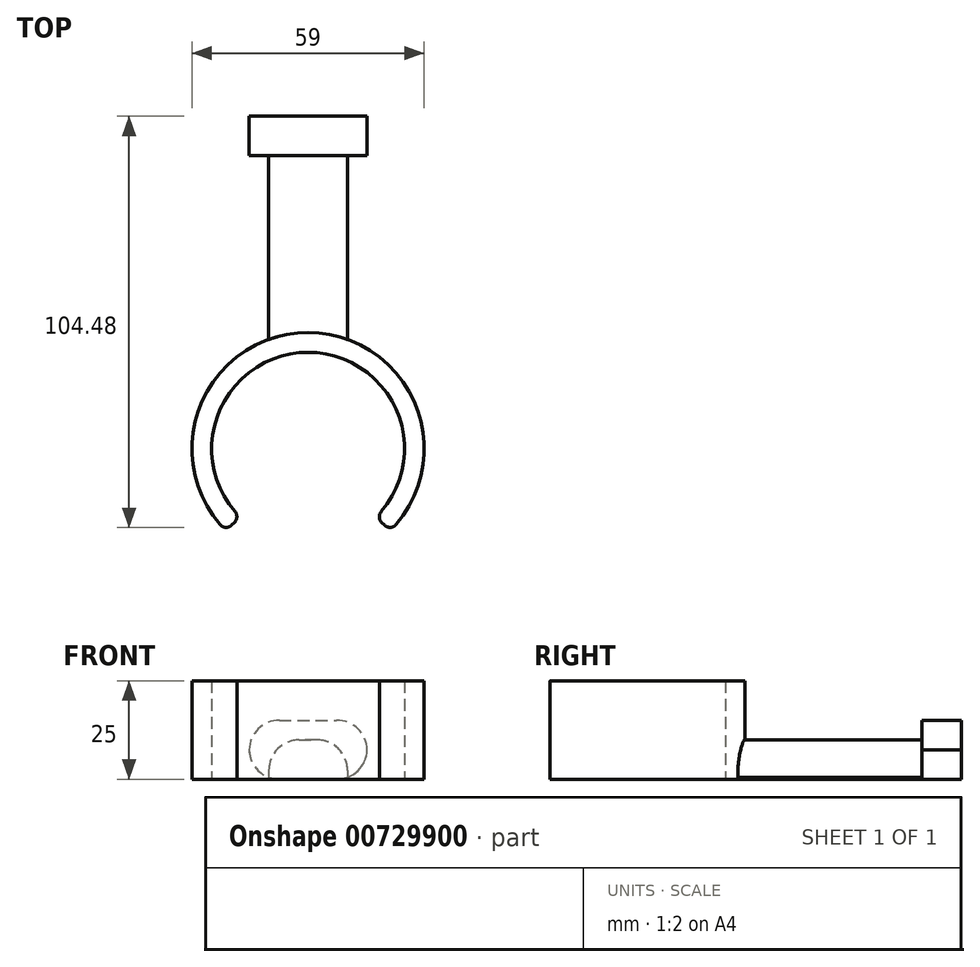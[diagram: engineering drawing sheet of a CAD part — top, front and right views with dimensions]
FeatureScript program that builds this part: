
annotation { "Feature Type Name" : "Feature", "Feature Type Description" : "" }
export const myFeature = defineFeature(function(context is Context, id is Id, definition is map)
    precondition{}
    {
        {
            var Q0;
            Q0=qCreatedBy(makeId("Top.planeOp"),FACE);
            var sketch = newSketch(context, id + "F0", { "sketchPlane" : qUnion([Q0])});
            skCircle(sketch, "E0", {"center": v(0, 0) * mm, "radius": 24.5 * mm});
            skCircle(sketch, "E1.0", {"center": v(0, 0) * mm, "radius": 29.5 * mm});
            skLineSegment(sketch, "E2.bottom", {"start": v(-10, 0) * mm, "end": v(10, 0) * mm});
            skLineSegment(sketch, "E2.top", {"start": v(-10, 74.5) * mm, "end": v(10, 74.5) * mm});
            skLineSegment(sketch, "E2.left", {"start": v(-10, 0) * mm, "end": v(-10, 74.5) * mm});
            skLineSegment(sketch, "E2.right", {"start": v(10, 0) * mm, "end": v(10, 74.5) * mm});
            skLineSegment(sketch, "E3", {"start": v(0, 0) * mm, "end": v(49.81, -49.81) * mm});
            skLineSegment(sketch, "E4", {"start": v(49.81, -49.81) * mm, "end": v(-49.81, -49.81) * mm});
            skLineSegment(sketch, "E5", {"start": v(-49.81, -49.81) * mm, "end": v(0, 0) * mm});
            skLineSegment(sketch, "E6.bottom", {"start": v(-15, 74.5) * mm, "end": v(15, 74.5) * mm});
            skLineSegment(sketch, "E6.top", {"start": v(-15, 84.5) * mm, "end": v(15, 84.5) * mm});
            skLineSegment(sketch, "E6.left", {"start": v(-15, 74.5) * mm, "end": v(-15, 84.5) * mm});
            skLineSegment(sketch, "E6.right", {"start": v(15, 74.5) * mm, "end": v(15, 84.5) * mm});
            skSolve(sketch);
        }
        {
            var Q0;
            {var subQ0=sQuery(id+"F0.wireOp",EDGE,"E2.right");var subQ1=sQuery(id+"F0.wireOp",EDGE,"E0");var subQ2=makeQuery(id+"F0.imprint","INTERSECT",VERTEX,{"derivedFrom":[subQ1,subQ0]});Q0=makeQuery(id+"F0.imprint","IMPRINT",FACE,{"disambiguationData":[TD([[makeQuery(id+"F0.imprint","IMPRINT",EDGE,{"disambiguationData":[TD([[subQ2,1.0]])],"derivedFrom":subQ1}),-1.0]])]});}
            var Q1;
            {var subQ0=sQuery(id+"F0.wireOp",EDGE,"E2.left");var subQ1=sQuery(id+"F0.wireOp",EDGE,"E0");var subQ2=makeQuery(id+"F0.imprint","INTERSECT",VERTEX,{"derivedFrom":[subQ1,subQ0]});Q1=makeQuery(id+"F0.imprint","IMPRINT",FACE,{"disambiguationData":[TD([[makeQuery(id+"F0.imprint","IMPRINT",EDGE,{"disambiguationData":[TD([[subQ2,1.0]])],"derivedFrom":subQ1}),-1.0]])]});}
            var Q2;
            {var subQ0=sQuery(id+"F0.wireOp",EDGE,"E2.left");var subQ1=sQuery(id+"F0.wireOp",EDGE,"E0");var subQ2=makeQuery(id+"F0.imprint","INTERSECT",VERTEX,{"derivedFrom":[subQ1,subQ0]});Q2=makeQuery(id+"F0.imprint","IMPRINT",FACE,{"disambiguationData":[TD([[makeQuery(id+"F0.imprint","IMPRINT",EDGE,{"disambiguationData":[TD([[subQ2,-1.0]])],"derivedFrom":subQ1}),-1.0]])]});}
            extrude(context, id + "F1", {"entities" : qUnion([Q0, Q1, Q2]), "depth" : 25 * mm, "offsetDistance" : 25 * mm});
        }
        {
            var Q0;
            Q0=makeQuery(id+"F1.opExtrude","SWEPT_EDGE",EDGE,{"disambiguationData":[OSD([sQuery(id+"F0.wireOp",EDGE,"E1.0"),sQuery(id+"F0.wireOp",EDGE,"E5")])]});
            var Q1;
            Q1=makeQuery(id+"F1.opExtrude","SWEPT_EDGE",EDGE,{"disambiguationData":[OSD([sQuery(id+"F0.wireOp",EDGE,"E0"),sQuery(id+"F0.wireOp",EDGE,"E5")])]});
            var Q2;
            Q2=makeQuery(id+"F1.opExtrude","SWEPT_EDGE",EDGE,{"disambiguationData":[OSD([sQuery(id+"F0.wireOp",EDGE,"E0"),sQuery(id+"F0.wireOp",EDGE,"E3")])]});
            var Q3;
            Q3=makeQuery(id+"F1.opExtrude","SWEPT_EDGE",EDGE,{"disambiguationData":[OSD([sQuery(id+"F0.wireOp",EDGE,"E1.0"),sQuery(id+"F0.wireOp",EDGE,"E3")])]});
            fillet(context, id + "F2", {"entities" : qUnion([Q0, Q1, Q2, Q3]), "radius" : 2 * mm, "tangentPropagation" : true, "allowEdgeOverflow" : false});
        }
        {
            var Q0;
            {var subQ0=sQuery(id+"F0.wireOp",EDGE,"E2.left");var subQ1=sQuery(id+"F0.wireOp",EDGE,"E1.0");var subQ2=makeQuery(id+"F0.imprint","INTERSECT",VERTEX,{"derivedFrom":[subQ1,subQ0]});Q0=makeQuery(id+"F0.imprint","IMPRINT",FACE,{"disambiguationData":[TD([[makeQuery(id+"F0.imprint","IMPRINT",EDGE,{"disambiguationData":[TD([[subQ2,1.0]])],"derivedFrom":subQ1}),-1.0]])]});}
            extrude(context, id + "F3", {"entities" : qUnion([Q0]), "operationType" : NewBodyOperationType.ADD, "depth" : 10 * mm, "offsetDistance" : 25 * mm});
        }
        {
            var Q0;
            Q0=makeQuery(id+"F0.imprint","IMPRINT",FACE,{"disambiguationData":[TD([[makeQuery(id+"F0.imprint","IMPRINT",EDGE,{"derivedFrom":sQuery(id+"F0.wireOp",EDGE,"E6.top")}),-1.0]])]});
            extrude(context, id + "F4", {"entities" : qUnion([Q0]), "operationType" : NewBodyOperationType.ADD, "depth" : 15 * mm, "offsetDistance" : 25 * mm});
        }
        {
            var Q0;
            Q0=makeQuery(id+"F3.opExtrude","CAP_EDGE",EDGE,{"disambiguationData":[OSD([sQuery(id+"F0.wireOp",EDGE,"E2.left")])],"isStart":false});
            var Q1;
            Q1=makeQuery(id+"F3.opExtrude","CAP_EDGE",EDGE,{"disambiguationData":[OSD([sQuery(id+"F0.wireOp",EDGE,"E2.right")])],"isStart":false});
            var Q2;
            Q2=makeQuery(id+"F4.opExtrude","CAP_EDGE",EDGE,{"disambiguationData":[OSD([sQuery(id+"F0.wireOp",EDGE,"E6.right")])],"isStart":false});
            var Q3;
            Q3=makeQuery(id+"F4.opExtrude","CAP_EDGE",EDGE,{"disambiguationData":[OSD([sQuery(id+"F0.wireOp",EDGE,"E6.left")])],"isStart":false});
            var Q4;
            Q4=makeQuery(id+"F4.opExtrude","CAP_EDGE",EDGE,{"disambiguationData":[OSD([sQuery(id+"F0.wireOp",EDGE,"E6.right")])],"isStart":true});
            var Q5;
            Q5=makeQuery(id+"F4.opExtrude","CAP_EDGE",EDGE,{"disambiguationData":[OSD([sQuery(id+"F0.wireOp",EDGE,"E6.left")])],"isStart":true});
            fillet(context, id + "F5", {"entities" : qUnion([Q0, Q1, Q2, Q3, Q4, Q5]), "radius" : 7.73 * mm, "tangentPropagation" : true, "allowEdgeOverflow" : false});
        }
    });
